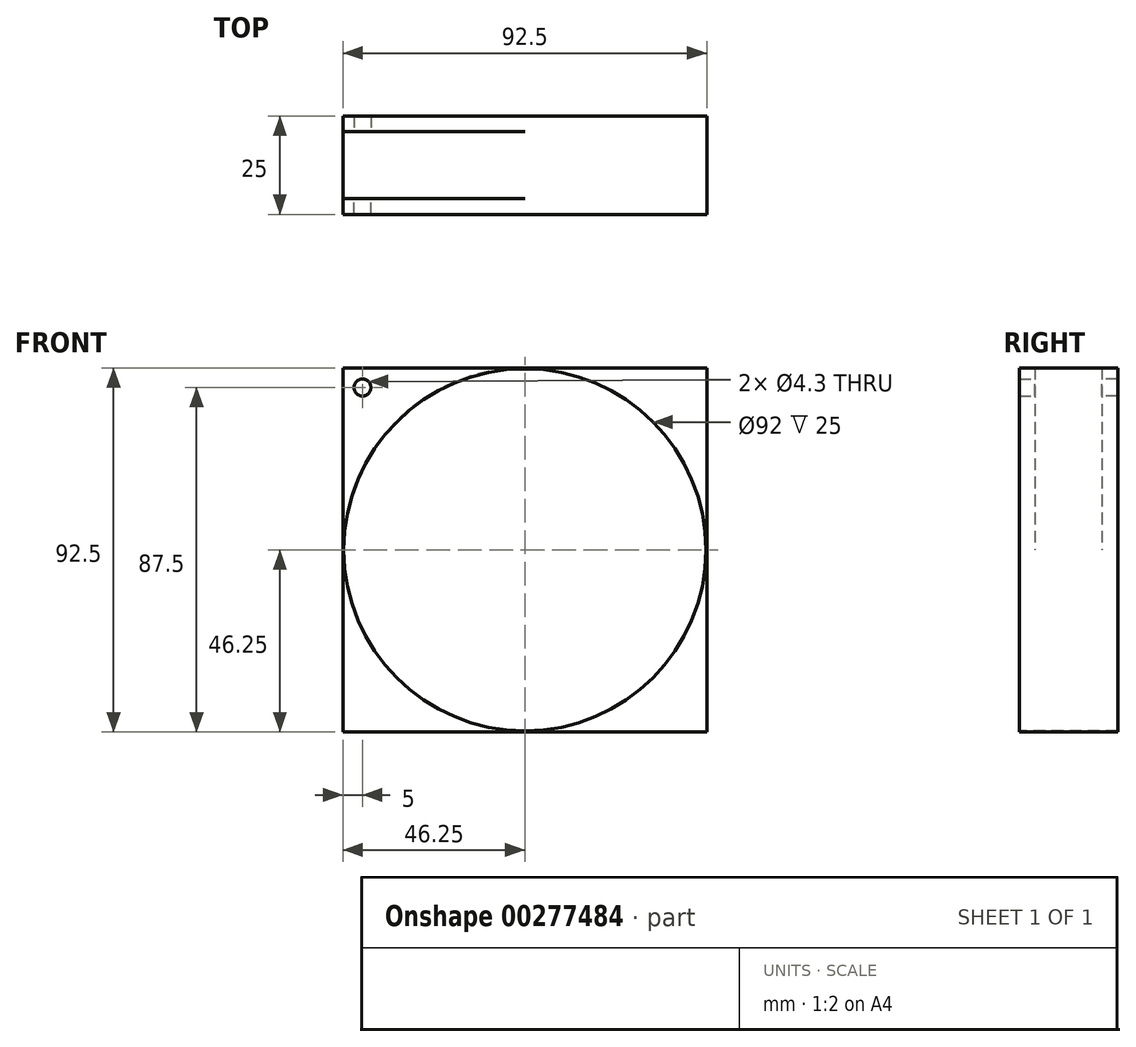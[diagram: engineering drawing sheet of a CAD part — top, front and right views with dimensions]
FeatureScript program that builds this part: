
annotation { "Feature Type Name" : "Feature", "Feature Type Description" : "" }
export const myFeature = defineFeature(function(context is Context, id is Id, definition is map)
    precondition{}
    {
        {
            var Q0;
            Q0=qCreatedBy(makeId("Front.planeOp"),FACE);
            var sketch = newSketch(context, id + "F7", { "sketchPlane" : qUnion([Q0])});
            skLineSegment(sketch, "E0.bottom", {"start": v(46.25, 46.25) * mm, "end": v(-46.25, 46.25) * mm});
            skLineSegment(sketch, "E0.top", {"start": v(46.25, -46.25) * mm, "end": v(-46.25, -46.25) * mm});
            skLineSegment(sketch, "E0.left", {"start": v(46.25, 46.25) * mm, "end": v(46.25, -46.25) * mm});
            skLineSegment(sketch, "E0.right", {"start": v(-46.25, 46.25) * mm, "end": v(-46.25, -46.25) * mm});
            skPoint(sketch, "E0.middle", {"position": v(0, 0) * mm});
            skSolve(sketch);
        }
        {
            var Q0;
            Q0=makeQuery(id+"F7.imprint","IMPRINT",FACE,{"disambiguationData":[TD([[makeQuery(id+"F7.imprint","IMPRINT",EDGE,{"derivedFrom":sQuery(id+"F7.wireOp",EDGE,"E0.bottom")}),1.0]])]});
            extrude(context, id + "F0", {"entities" : qUnion([Q0]), "endBound" : BoundingType.SYMMETRIC, "depth" : 25 * mm});
        }
        {
            var Q0;
            Q0=qCreatedBy(makeId("Front.planeOp"),FACE);
            var sketch = newSketch(context, id + "F1", { "sketchPlane" : qUnion([Q0])});
            skCircle(sketch, "E1", {"center": v(0, 0) * mm, "radius": 46 * mm});
            skSolve(sketch);
        }
        {
            var Q0;
            Q0 = qSketchRegion(id + "F1", true);
            extrude(context, id + "F8", {"entities" : qUnion([Q0]), "operationType" : NewBodyOperationType.REMOVE, "endBound" : BoundingType.SYMMETRIC, "oppositeDirection" : true, "depth" : 25 * mm});
        }
        {
            var Q0;
            Q0=qCreatedBy(makeId("Front.planeOp"),FACE);
            var sketch = newSketch(context, id + "F2", { "sketchPlane" : qUnion([Q0])});
            skArc(sketch, "E2", {"start": v(0, 46.25) * mm, "mid": v(-32.7, 32.7) * mm, "end": v(-46.25, 0) * mm});
            skLineSegment(sketch, "E3.0", {"start": v(-46.25, 46.25) * mm, "end": v(-46.25, 0) * mm});
            skLineSegment(sketch, "E4.0", {"start": v(0, 46.25) * mm, "end": v(-46.25, 46.25) * mm});
            skPoint(sketch, "E5.orphan", {"position": v(46.25, 46.25) * mm});
            skPoint(sketch, "E6.trimOffspring.end.orphan", {"position": v(-46.25, -46.25) * mm});
            skSolve(sketch);
        }
        {
            var Q0;
            Q0 = qSketchRegion(id + "F2", true);
            extrude(context, id + "F3", {"entities" : qUnion([Q0]), "operationType" : NewBodyOperationType.REMOVE, "endBound" : BoundingType.SYMMETRIC, "depth" : 17 * mm});
        }
        {
            var Q0;
            Q0=qCreatedBy(makeId("Front.planeOp"),FACE);
            var sketch = newSketch(context, id + "F4", { "sketchPlane" : qUnion([Q0])});
            skLineSegment(sketch, "E7.0", {"start": v(46.25, 46.25) * mm, "end": v(-46.25, 46.25) * mm});
            skLineSegment(sketch, "E8.0", {"start": v(-46.25, 46.25) * mm, "end": v(-46.25, -46.25) * mm});
            skPoint(sketch, "E9", {"position": v(-41.25, 41.25) * mm});
            skSolve(sketch);
        }
        {
            var Q0;
            Q0=sQuery(id+"F4.wireOp",VERTEX,"E9");
            var Q1;
            Q1=makeQuery(id+"F0.opExtrude","SWEPT_BODY",BODY,{"disambiguationData":[OSD([sQuery(id+"F7.wireOp",EDGE,"E0.bottom"),sQuery(id+"F7.wireOp",EDGE,"E0.top"),sQuery(id+"F7.wireOp",EDGE,"E0.left"),sQuery(id+"F7.wireOp",EDGE,"E0.right")])]});
            hole(context, id + "F5", {"style" : HoleStyle.SIMPLE, "endStyle" : HoleEndStyle.THROUGH, "holeDiameter" : 4.3 * mm, "tappedDepth" : 12 * mm, "tapClearance" : 3, "locations" : qUnion([Q0]), "scope" : qUnion([Q1])});
        }
        {
            var Q0;
            Q0=sQuery(id+"F4.wireOp",VERTEX,"E9");
            var Q1;
            Q1=makeQuery(id+"F0.opExtrude","SWEPT_BODY",BODY,{"disambiguationData":[OSD([sQuery(id+"F7.wireOp",EDGE,"E0.bottom"),sQuery(id+"F7.wireOp",EDGE,"E0.top"),sQuery(id+"F7.wireOp",EDGE,"E0.left"),sQuery(id+"F7.wireOp",EDGE,"E0.right")])]});
            hole(context, id + "F6", {"style" : HoleStyle.SIMPLE, "endStyle" : HoleEndStyle.THROUGH, "oppositeDirection" : true, "holeDiameter" : 4.3 * mm, "tappedDepth" : 12 * mm, "tapClearance" : 3, "locations" : qUnion([Q0]), "scope" : qUnion([Q1])});
        }
    });
